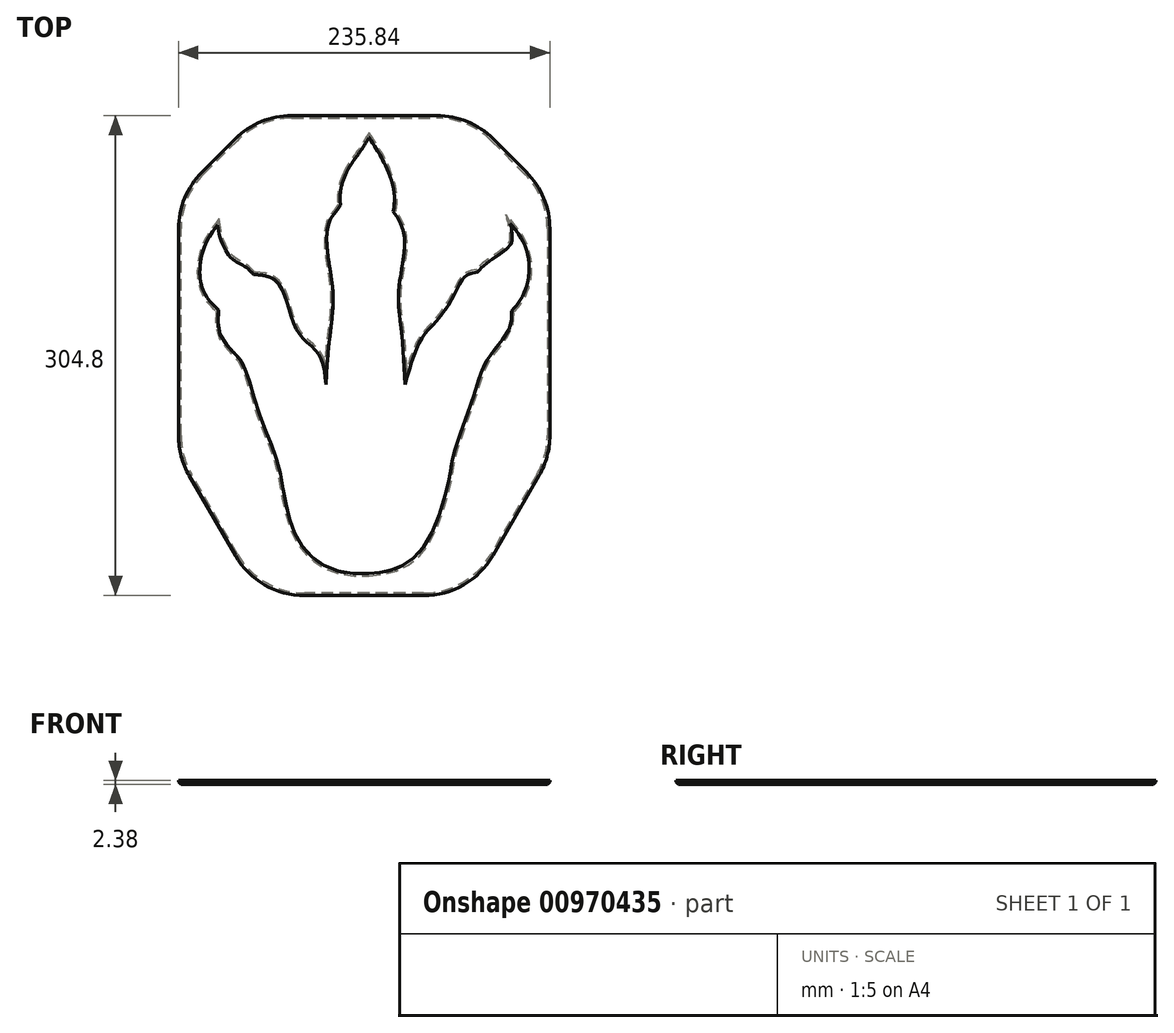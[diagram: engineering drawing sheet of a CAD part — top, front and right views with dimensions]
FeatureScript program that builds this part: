
annotation { "Feature Type Name" : "Feature", "Feature Type Description" : "" }
export const myFeature = defineFeature(function(context is Context, id is Id, definition is map)
    precondition{}
    {
        {
            var Q0;
            Q0=qCreatedBy(makeId("Top.planeOp"),FACE);
            var sketch = newSketch(context, id + "F0", { "sketchPlane" : qUnion([Q0])});
            skFitSpline(sketch, "E0", {"points": [v(0, 155.88) * mm, v(-8.08, 143.36) * mm, v(-16.27, 128.9) * mm, v(-18.68, 112.06) * mm, v(-25.9, 101.46) * mm, v(-26.38, 76.42) * mm, v(-23.5, 52.82) * mm, v(-26.38, 22) * mm, v(-28.79, -18.93) * mm], "startDerivative": vector(-74.24, -121.24) * mm, "endDerivative": vector(-9.2, -245.94) * mm});
            skFitSpline(sketch, "E1", {"points": [v(-26.39, -16.91) * mm, v(-31.74, 15.2) * mm, v(-46.7, 32.55) * mm, v(-59.22, 62.94) * mm, v(-82.1, 67.27) * mm], "startDerivative": vector(-24.33, 117.64) * mm, "endDerivative": vector(-110.03, -5.95) * mm});
            skFitSpline(sketch, "E2", {"points": [v(-71, 64.06) * mm, v(-79.66, 72.72) * mm, v(-88.85, 78.76) * mm, v(-96.73, 97.14) * mm, v(-96.73, 108.96) * mm], "startDerivative": vector(-34.79, 41.37) * mm, "endDerivative": vector(5.02, 45.67) * mm});
            skFitSpline(sketch, "E3", {"points": [v(-94.74, 101.82) * mm, v(-105.6, 84.37) * mm, v(-105.98, 57.26) * mm, v(-86.04, 37.56) * mm], "startDerivative": vector(-41.16, -51.4) * mm, "endDerivative": vector(69.67, -48.45) * mm});
            skFitSpline(sketch, "E4", {"points": [v(-95.4, 50.41) * mm, v(-95.66, 30.66) * mm, v(-86.21, 17.56) * mm, v(-80.08, 9.04) * mm, v(-70.12, -21.74) * mm, v(-58.98, -51.44) * mm, v(-53.23, -79.66) * mm, v(-42.87, -105.21) * mm, v(-20.94, -120.57) * mm, v(9.25, -121.62) * mm], "startDerivative": vector(-34.09, -207.37) * mm, "endDerivative": vector(252.38, 19.67) * mm});
            skFitSpline(sketch, "E5", {"points": [v(-0.98, -122.3) * mm, v(17.67, -118.55) * mm, v(37.58, -99.57) * mm, v(50.84, -58.3) * mm, v(52.58, -48.23) * mm, v(67.33, -4.3) * mm, v(74.7, 14.18) * mm, v(87.54, 31.52) * mm, v(89.92, 44.19) * mm, v(87.72, 53.78) * mm], "startDerivative": vector(181.74, 17.92) * mm, "endDerivative": vector(-37.63, 124.35) * mm});
            skFitSpline(sketch, "E6", {"points": [v(85.08, 39.88) * mm, v(97.65, 55.62) * mm, v(99.04, 83.9) * mm, v(80.28, 109.18) * mm], "startDerivative": vector(49.48, 46.52) * mm, "endDerivative": vector(-63.95, 63.94) * mm});
            skFitSpline(sketch, "E7", {"points": [v(87.72, 105.63) * mm, v(90.2, 91.56) * mm, v(87.72, 84.9) * mm, v(71.4, 72.62) * mm, v(64, 61.52) * mm], "startDerivative": vector(13.83, -59.98) * mm, "endDerivative": vector(-21.16, -45.02) * mm});
            skFitSpline(sketch, "E8", {"points": [v(73.91, 69.51) * mm, v(62.66, 67.88) * mm, v(57.19, 62.4) * mm, v(51.12, 50.57) * mm, v(40.61, 36.36) * mm, v(32.62, 26.89) * mm, v(25.66, 9.99) * mm, v(18.57, -16.1) * mm], "startDerivative": vector(-99.82, -3.59) * mm, "endDerivative": vector(-35.92, -140.6) * mm});
            skFitSpline(sketch, "E9", {"points": [v(22.4, -8.72) * mm, v(20, 30.11) * mm, v(18.2, 58.92) * mm, v(21.29, 94) * mm, v(5.5, 117.61) * mm], "startDerivative": vector(-6.22, 149.61) * mm, "endDerivative": vector(-89.44, 91.47) * mm});
            skFitSpline(sketch, "E10", {"points": [v(13.08, 100.76) * mm, v(15.24, 119.16) * mm, v(8.75, 138.79) * mm, v(4.11, 147.12) * mm, v(-4.05, 160) * mm], "startDerivative": vector(16.12, 65.25) * mm, "endDerivative": vector(-36.3, 56.68) * mm});
            skFitSpline(sketch, "E11", {"points": [v(-18.04, 104.5) * mm, v(-18.68, 121.57) * mm, v(-13.33, 135.73) * mm], "startDerivative": vector(-4.44, 34.18) * mm, "endDerivative": vector(14.2, 28.15) * mm});
            skFitSpline(sketch, "E12.trimOffspring", {"points": [v(0, 155.88) * mm, v(-8.08, 143.36) * mm, v(-16.27, 128.9) * mm, v(-18.68, 112.06) * mm, v(-25.9, 101.46) * mm, v(-26.38, 76.42) * mm, v(-23.5, 52.82) * mm, v(-26.38, 22) * mm, v(-28.79, -18.93) * mm], "startDerivative": vector(-74.24, -121.24) * mm, "endDerivative": vector(-9.2, -245.94) * mm});
            skLineSegment(sketch, "E13.bottom", {"start": v(-121.75, 168.55) * mm, "end": v(114.1, 168.55) * mm});
            skLineSegment(sketch, "E13.top", {"start": v(-121.75, -136.25) * mm, "end": v(114.1, -136.25) * mm});
            skLineSegment(sketch, "E13.left", {"start": v(-121.75, 168.55) * mm, "end": v(-121.75, -136.25) * mm});
            skLineSegment(sketch, "E13.right", {"start": v(114.1, 168.55) * mm, "end": v(114.1, -136.25) * mm});
            skSolve(sketch);
        }
        {
            var Q0;
            Q0=makeQuery(id+"F0.imprint","IMPRINT",FACE,{"disambiguationData":[TD([[makeQuery(id+"F0.imprint","IMPRINT",EDGE,{"derivedFrom":sQuery(id+"F0.wireOp",EDGE,"E1")}),-1.0]])]});
            extrude(context, id + "F1", {"entities" : qUnion([Q0]), "depth" : 2.38 * mm, "offsetDistance" : 25.4 * mm});
        }
        {
            var Q0;
            Q0=makeQuery(id+"F1.opExtrude","SWEPT_EDGE",EDGE,{"disambiguationData":[OSD([sQuery(id+"F0.wireOp",EDGE,"E13.top"),sQuery(id+"F0.wireOp",EDGE,"E13.left")])]});
            var Q1;
            Q1=makeQuery(id+"F1.opExtrude","SWEPT_EDGE",EDGE,{"disambiguationData":[OSD([sQuery(id+"F0.wireOp",EDGE,"E13.top"),sQuery(id+"F0.wireOp",EDGE,"E13.right")])]});
            chamfer(context, id + "F2", {"entities" : qUnion([Q0, Q1]), "chamferType" : ChamferType.OFFSET_ANGLE, "width" : 50.8 * mm, "oppositeDirection" : false, "angle" : 60 * degree, "tangentPropagation" : true});
        }
        {
            var Q0;
            Q0=makeQuery(id+"F1.opExtrude","SWEPT_EDGE",EDGE,{"disambiguationData":[OSD([sQuery(id+"F0.wireOp",EDGE,"E13.bottom"),sQuery(id+"F0.wireOp",EDGE,"E13.left")])]});
            var Q1;
            Q1=makeQuery(id+"F1.opExtrude","SWEPT_EDGE",EDGE,{"disambiguationData":[OSD([sQuery(id+"F0.wireOp",EDGE,"E13.bottom"),sQuery(id+"F0.wireOp",EDGE,"E13.right")])]});
            chamfer(context, id + "F3", {"entities" : qUnion([Q0, Q1]), "width" : 50.8 * mm, "tangentPropagation" : true});
        }
        {
            var Q0;
            {var subQ0=sQuery(id+"F0.wireOp",EDGE,"E13.left");Q0=makeQuery(id+"F3.opChamfer","BLEND_EDGE",EDGE,{"blendedFrom":[makeQuery(id+"F1.opExtrude","SWEPT_EDGE",EDGE,{"disambiguationData":[OSD([sQuery(id+"F0.wireOp",EDGE,"E13.bottom"),subQ0])]}),makeQuery(id+"F1.opExtrude","SWEPT_FACE",FACE,{"disambiguationData":[OSD([subQ0])]})],"blendedInto":[makeQuery(id+"F1.opExtrude","SWEPT_FACE",FACE,{"disambiguationData":[OSD([subQ0])]})]});}
            var Q1;
            {var subQ0=sQuery(id+"F0.wireOp",EDGE,"E13.bottom");Q1=makeQuery(id+"F3.opChamfer","BLEND_EDGE",EDGE,{"blendedFrom":[makeQuery(id+"F1.opExtrude","SWEPT_EDGE",EDGE,{"disambiguationData":[OSD([subQ0,sQuery(id+"F0.wireOp",EDGE,"E13.left")])]}),makeQuery(id+"F1.opExtrude","SWEPT_FACE",FACE,{"disambiguationData":[OSD([subQ0])]})],"blendedInto":[makeQuery(id+"F1.opExtrude","SWEPT_FACE",FACE,{"disambiguationData":[OSD([subQ0])]})]});}
            var Q2;
            {var subQ0=sQuery(id+"F0.wireOp",EDGE,"E13.bottom");Q2=makeQuery(id+"F3.opChamfer","BLEND_EDGE",EDGE,{"blendedFrom":[makeQuery(id+"F1.opExtrude","SWEPT_EDGE",EDGE,{"disambiguationData":[OSD([subQ0,sQuery(id+"F0.wireOp",EDGE,"E13.right")])]}),makeQuery(id+"F1.opExtrude","SWEPT_FACE",FACE,{"disambiguationData":[OSD([subQ0])]})],"blendedInto":[makeQuery(id+"F1.opExtrude","SWEPT_FACE",FACE,{"disambiguationData":[OSD([subQ0])]})]});}
            var Q3;
            {var subQ0=sQuery(id+"F0.wireOp",EDGE,"E13.right");Q3=makeQuery(id+"F3.opChamfer","BLEND_EDGE",EDGE,{"blendedFrom":[makeQuery(id+"F1.opExtrude","SWEPT_EDGE",EDGE,{"disambiguationData":[OSD([sQuery(id+"F0.wireOp",EDGE,"E13.bottom"),subQ0])]}),makeQuery(id+"F1.opExtrude","SWEPT_FACE",FACE,{"disambiguationData":[OSD([subQ0])]})],"blendedInto":[makeQuery(id+"F1.opExtrude","SWEPT_FACE",FACE,{"disambiguationData":[OSD([subQ0])]})]});}
            var Q4;
            {var subQ0=sQuery(id+"F0.wireOp",EDGE,"E13.right");Q4=makeQuery(id+"F2.opChamfer","BLEND_EDGE",EDGE,{"blendedFrom":[makeQuery(id+"F1.opExtrude","SWEPT_EDGE",EDGE,{"disambiguationData":[OSD([sQuery(id+"F0.wireOp",EDGE,"E13.top"),subQ0])]}),makeQuery(id+"F1.opExtrude","SWEPT_FACE",FACE,{"disambiguationData":[OSD([subQ0])]})],"blendedInto":[makeQuery(id+"F1.opExtrude","SWEPT_FACE",FACE,{"disambiguationData":[OSD([subQ0])]})]});}
            var Q5;
            {var subQ0=sQuery(id+"F0.wireOp",EDGE,"E13.top");Q5=makeQuery(id+"F2.opChamfer","BLEND_EDGE",EDGE,{"blendedFrom":[makeQuery(id+"F1.opExtrude","SWEPT_EDGE",EDGE,{"disambiguationData":[OSD([subQ0,sQuery(id+"F0.wireOp",EDGE,"E13.right")])]}),makeQuery(id+"F1.opExtrude","SWEPT_FACE",FACE,{"disambiguationData":[OSD([subQ0])]})],"blendedInto":[makeQuery(id+"F1.opExtrude","SWEPT_FACE",FACE,{"disambiguationData":[OSD([subQ0])]})]});}
            var Q6;
            {var subQ0=sQuery(id+"F0.wireOp",EDGE,"E13.top");Q6=makeQuery(id+"F2.opChamfer","BLEND_EDGE",EDGE,{"blendedFrom":[makeQuery(id+"F1.opExtrude","SWEPT_EDGE",EDGE,{"disambiguationData":[OSD([subQ0,sQuery(id+"F0.wireOp",EDGE,"E13.left")])]}),makeQuery(id+"F1.opExtrude","SWEPT_FACE",FACE,{"disambiguationData":[OSD([subQ0])]})],"blendedInto":[makeQuery(id+"F1.opExtrude","SWEPT_FACE",FACE,{"disambiguationData":[OSD([subQ0])]})]});}
            var Q7;
            {var subQ0=sQuery(id+"F0.wireOp",EDGE,"E13.left");Q7=makeQuery(id+"F2.opChamfer","BLEND_EDGE",EDGE,{"blendedFrom":[makeQuery(id+"F1.opExtrude","SWEPT_EDGE",EDGE,{"disambiguationData":[OSD([sQuery(id+"F0.wireOp",EDGE,"E13.top"),subQ0])]}),makeQuery(id+"F1.opExtrude","SWEPT_FACE",FACE,{"disambiguationData":[OSD([subQ0])]})],"blendedInto":[makeQuery(id+"F1.opExtrude","SWEPT_FACE",FACE,{"disambiguationData":[OSD([subQ0])]})]});}
            fillet(context, id + "F4", {"entities" : qUnion([Q0, Q1, Q2, Q3, Q4, Q5, Q6, Q7]), "radius" : 50.8 * mm, "tangentPropagation" : true, "allowEdgeOverflow" : false});
        }
        {
            var Q0;
            Q0=makeQuery(id+"F1.opExtrude","CAP_FACE",FACE,{"disambiguationData":[OSD([sQuery(id+"F0.wireOp",EDGE,"E0"),sQuery(id+"F0.wireOp",EDGE,"E1"),sQuery(id+"F0.wireOp",EDGE,"E2"),sQuery(id+"F0.wireOp",EDGE,"E3"),sQuery(id+"F0.wireOp",EDGE,"E4"),sQuery(id+"F0.wireOp",EDGE,"E5"),sQuery(id+"F0.wireOp",EDGE,"E6"),sQuery(id+"F0.wireOp",EDGE,"E7"),sQuery(id+"F0.wireOp",EDGE,"E8"),sQuery(id+"F0.wireOp",EDGE,"E9"),sQuery(id+"F0.wireOp",EDGE,"E10"),sQuery(id+"F0.wireOp",EDGE,"E11"),sQuery(id+"F0.wireOp",EDGE,"E12.trimOffspring"),sQuery(id+"F0.wireOp",EDGE,"E13.bottom"),sQuery(id+"F0.wireOp",EDGE,"E13.top"),sQuery(id+"F0.wireOp",EDGE,"E13.left"),sQuery(id+"F0.wireOp",EDGE,"E13.right")])],"isStart":true});
            chamfer(context, id + "F5", {"entities" : qUnion([Q0]), "width" : 1.59 * mm, "tangentPropagation" : true});
        }
    });
